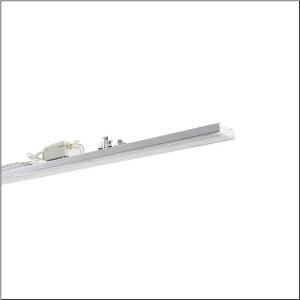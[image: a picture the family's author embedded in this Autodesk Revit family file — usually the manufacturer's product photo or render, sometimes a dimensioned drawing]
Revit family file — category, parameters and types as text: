
# Revit family: licross_r__21_recessed_ho_52te1edv4l2s_2def
name_source: partatom
category: Lighting Fixtures
units: mm (PartAtom-declared; Revit-internal decimal feet)

## family parameters
Cut with Voids When Loaded = No
Host = Face
Light Source = No
Part Type = Normal
Room Calculation Point = No
Round Connector Dimension = Use Diameter
Shared = No

## types (1)
- --- (1 x LED, 22130 lm, 125.6 W, 4000K)
    Apparent Load = 126 VA
    CIE Flux Codes = 85 95 99 100 100
    Color Rendering = 80
    Color Temperature = 4000K
    Default Elevation = 1800 mm
    Description = Licross® 21 Recessed HO, luminaire insert, of sheet steel, galvanised, coil coated, white, length: 2.250mm, width: 66mm, height: 67mm, LED rated luminous flux: 22.130lm, light colour: 840, control gear: DALI 2, with plug, 5-pole, with phase selection, mains connection: 220..240V, AC, 50/60Hz, rated input power: 126W, halogen-free wiring, primary light control with lens, of plastic, primary optical cover: cover, of PMMA, light emission: direct distribution, primary light characteristic: symmetric, protection rating (complete): IP54, insulation class (complete): insulation class I (protective earthing), certification: CE, ENEC, VDE, UKCA, protection symbol: D if used in an environment with non-conductive dust loads with corresponding accessories, impact resistance: IK06, permissible ambient temperature for indoor applications: -40..+30°C, corresponds to IFS (International Featured Standards) requirements for safety and quality in the food industry, reducing of maximum allowable ambient temperature of 5°C with ceiling mounting, LABS conformity tested according to VDMA 24364:2018-05, packaging unit: 1 piece
    Height = 58 mm
    Lamp = 1 x LED
    Lamp Light Flux = 22130 lm
    Lamp Power = 125.6 W
    Lamp count = 1
    Length = 2250 mm
    Luminous efficacy = 176 lm/W
    Manufacturer = Siteco
    ModVariant = No
    Model = 52TE1EDV4L2S
    Mounting Place = Ceiling
    Mounting Type = Pendant
    Number of Poles = 1
    OnlyDefault = Yes
    Power Factor = 1
    Product Name = Licross® 21 Recessed HO
    Product group = luminaire insert
    ProductGroupID = 901
    Protection Class = Protection class I
    Protection Degree = IP 54
    RLX_Detail_Level = 1
    RLX_Emergency_Light_Flux = 0 lm
    RLX_Emergency_Type = 0
    RLX_Emergency_Type_DB = No
    RlxData = <blob elided: 29605 chars, md5=b6a9f3f4>
    Socket = socket
    Standby Power = 0 W
    System Light Flux = 22129 lm
    System Power = 126 W
    Type Comments = factory setting: luminous flux: 100 % | dim-lin: 254 | 489 mA
    Type Image = l_1296930.jpg
    URL = http://relux.com
    VarID = @adj_056957
    Voltage = 0 V
    Weight = 0.00 kg
    Width = 66 mm

## geometry (parser evidence)
native form markers: Blend x4, Sweep x8
no freeform markers — native parametric forms only
